# Revit family: 2.Радиальный вентилятор с назад загнутыми лопатками WNP
name_source: partatom
category: Оборудование
revit_build: Autodesk Revit 2016 (Build: 20151209_0715(x64)
units: mm (PartAtom-declared; Revit-internal decimal feet)

## family parameters
Всегда вертикально = Да
На основе рабочей плоскости = Нет
Общий = Нет
При загрузке вырезать с полостями = Нет
Размер круглого соединителя = Использовать диаметр
Тип детали = Нормальный
Точка расчета площади = Нет

## types (19) — shared parameters
Единица измерения = шт.
Завод изготовитель = KORF
Ключевая пометка = Вентиляция
Материал = Сталь серая
Наименование и тех.хар-ка = Радиальный вентилятор с назад загнутыми лопатками
Раздел = ОВ

## per-type parameters (varying)
| type | А | Б | Высота | Г | Д | Е | Ж | И | И1 | М | Масса единицы | Мощность двигателя N,Вт | Напряжение U,В | Размер В | Сила тока J, А | Тип, марка, обозначение | Частота вращения n, об/мин | Ширина |
| 40-20/18 | 400 мм | 200 мм | 200 мм | 220 мм | 440 мм | 240 мм | 243 мм | 358 мм | 318 мм | 9 мм | 14.5 кг | 250 | 3х230/3х400 | 420 мм | 0.7 | WNP 40-20/18.2D | 2710 | 400 мм |
| 50-25/20 | 500 мм | 250 мм | 250 мм | 270 мм | 540 мм | 290 мм | 293 мм | 416 мм | 376 мм | 9 мм | 18 кг | 250 | 3х230/3х400 | 520 мм | 0.7 | WNP 50-25/20.2D | 2710 | 500 мм |
| 50-25/22 | 500 мм | 250 мм | 250 мм | 270 мм | 540 мм | 290 мм | 293 мм | 416 мм | 376 мм | 9 мм | 19.5 кг | 550 | 3х230/3х400 | 520 мм | 1.42 | WNP 50-25/22.2D | 2760 | 500 мм |
| 50-30/22 | 500 мм | 300 мм | 300 мм | 320 мм | 540 мм | 340 мм | 343 мм | 458 мм | 418 мм | 9 мм | 25.5 кг | 550 | 3х230/3х400 | 520 мм | 1.42 | WNP 50-30/22.2D | 2760 | 500 мм |
| 50-30/25 | 500 мм | 300 мм | 300 мм | 320 мм | 540 мм | 340 мм | 343 мм | 458 мм | 418 мм | 9 мм | 27.7 кг | 750 | 3х230/3х400 | 520 мм | 1.83 | WNP 50-30/25.2D | 2730 | 500 мм |
| 60-30/25 | 600 мм | 300 мм | 300 мм | 320 мм | 640 мм | 340 мм | 343 мм | 498 мм | 458 мм | 9 мм | 31 кг | 750 | 3х230/3х400 | 620 мм | 1.83 | WNP 60-30/25.2D | 2730 | 600 мм |
| 60-30/28 | 600 мм | 300 мм | 300 мм | 320 мм | 640 мм | 340 мм | 343 мм | 498 мм | 458 мм | 9 мм | 37 кг | 1100 | 3х230/3х400 | 620 мм | 2.51 | WNP 60-30/28.2D | 2770 | 600 мм |
| 60-35/28 | 600 мм | 350 мм | 350 мм | 370 мм | 640 мм | 390 мм | 393 мм | 498 мм | 458 мм | 9 мм | 39 кг | 1100 | 3х230/3х400 | 620 мм | 2.51 | WNP 60-35/28.2D | 2770 | 600 мм |
| 60-35/31 | 600 мм | 350 мм | 350 мм | 370 мм | 640 мм | 390 мм | 393 мм | 498 мм | 458 мм | 9 мм | 39,5 кг | 1500 | 3х230/3х400 | 620 мм | 3,32 | WNP 60-35/31.2D | 2800 | 600 мм |
| 70-40/31M | 700 мм | 400 мм | 400 мм | 420 мм | 740 мм | 440 мм | 443 мм | 568 мм | 528 мм | 9 мм | 47 кг | 1500 | 3х230/3х400 | 720 мм | 3,32 | WNP 70-40/31.2DM | 2800 | 700 мм |
| 70-40/31 | 700 мм | 400 мм | 400 мм | 420 мм | 740 мм | 440 мм | 443 мм | 568 мм | 528 мм | 9 мм | 51 кг | 2200 | 3х230/3х400 | 720 мм | 4.61 | WNP 70-40/31.2D | 2840 | 700 мм |
| 70-40/35 | 700 мм | 400 мм | 400 мм | 420 мм | 740 мм | 440 мм | 443 мм | 568 мм | 528 мм | 9 мм | 52.5 кг | 3000 | 3х230/3х400 | 720 мм | 6.1 | WNP 70-40/35.2D | 2840 | 700 мм |
| 80-50/35 | 800 мм | 500 мм | 500 мм | 520 мм | 840 мм | 540 мм | 543 мм | 635 мм | 595 мм | 9 мм | 60.5 кг | 3000 | 3х230/3х400 | 820 мм | 6.1 | WNP 80-50/35.2D | 2840 | 800 мм |
| 80-50/40 | 800 мм | 500 мм | 500 мм | 520 мм | 840 мм | 540 мм | 543 мм | 635 мм | 595 мм | 9 мм | 70 кг | 3000 | 3х230/3х400 | 820 мм | 6.47 | WNP 80-50/40.4D | 1420 | 800 мм |
| 90-50/35 | 900 мм | 500 мм | 510 мм | 530 мм | 960 мм | 560 мм | 553 мм | 650 мм | 610 мм | 11 мм | 65.5 кг | 3000 | 3х230/3х400 | 930 мм | 6.1 | WNP 90-50/35.2D | 2840 | 920 мм |
| 90-50/40 | 900 мм | 500 мм | 510 мм | 530 мм | 960 мм | 560 мм | 553 мм | 650 мм | 610 мм | 11 мм | 75 кг | 5500 | 3х400/3х690 | 930 мм | 10.53 | WNP 90-50/40.2D | 2880 | 920 мм |
| 90-50/40 4D | 900 мм | 500 мм | 510 мм | 530 мм | 960 мм | 560 мм | 553 мм | 650 мм | 610 мм | 11 мм | 78 кг | 3000 | 3х230/3х400 | 930 мм | 6.47 | WNP 90-50/40.4D | 1420 | 920 мм |
| 100-50/40 | 1000 мм | 500 мм | 510 мм | 530 мм | 1060 мм | 560 мм | 553 мм | 670 мм | 630 мм | 11 мм | 85.5 кг | 5500 | 3х400/3х690 | 1030 мм | 10.53 | WNP 100-50/40.2D | 2880 | 1020 мм |
| 100-50/45 | 1000 мм | 500 мм | 510 мм | 530 мм | 1060 мм | 560 мм | 553 мм | 670 мм | 630 мм | 11 мм | 87 кг | 4000 | 3х400/3х690 | 1030 мм | 8.26 | WNP 100-50/45.4D | 1430 | 1020 мм |
